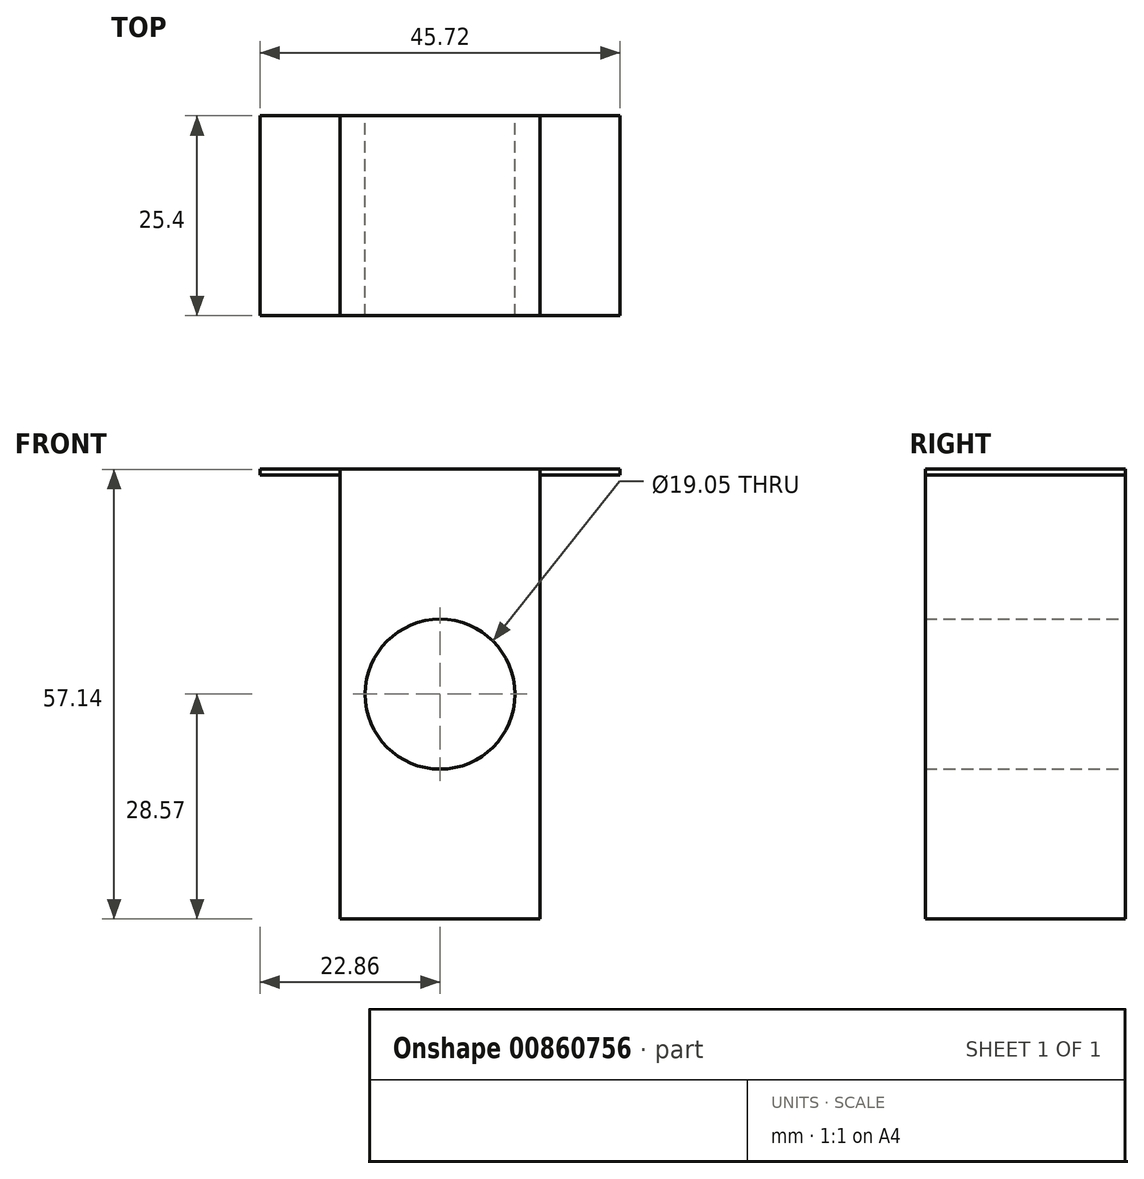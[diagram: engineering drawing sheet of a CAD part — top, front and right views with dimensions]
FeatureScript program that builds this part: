
annotation { "Feature Type Name" : "Feature", "Feature Type Description" : "" }
export const myFeature = defineFeature(function(context is Context, id is Id, definition is map)
    precondition{}
    {
        {
            var Q0;
            Q0=qCreatedBy(makeId("Front.planeOp"),FACE);
            var sketch = newSketch(context, id + "F0", { "sketchPlane" : qUnion([Q0])});
            skLineSegment(sketch, "E0.bottom", {"start": v(12.7, -28.58) * mm, "end": v(-12.7, -28.58) * mm});
            skLineSegment(sketch, "E0.top", {"start": v(12.7, 28.58) * mm, "end": v(-12.7, 28.58) * mm});
            skLineSegment(sketch, "E0.left", {"start": v(12.7, -28.58) * mm, "end": v(12.7, 28.57) * mm});
            skLineSegment(sketch, "E0.right", {"start": v(-12.7, -28.58) * mm, "end": v(-12.7, 28.57) * mm});
            skPoint(sketch, "E0.middle", {"position": v(0, 0) * mm});
            skSolve(sketch);
        }
        {
            var Q0;
            Q0 = qSketchRegion(id + "F0", true);
            extrude(context, id + "F1", {"entities" : qUnion([Q0]), "depth" : 25.4 * mm, "offsetDistance" : 25.4 * mm});
        }
        {
            var Q0;
            Q0=makeQuery(id+"F1.opExtrude","SWEPT_FACE",FACE,{"disambiguationData":[OSD([sQuery(id+"F0.wireOp",EDGE,"E0.top")])]});
            var sketch = newSketch(context, id + "F2", { "sketchPlane" : qUnion([Q0])});
            skLineSegment(sketch, "E1", {"start": v(12.7, 0) * mm, "end": v(22.86, 0) * mm});
            skLineSegment(sketch, "E2", {"start": v(22.86, 0) * mm, "end": v(22.86, -25.4) * mm});
            skLineSegment(sketch, "E3", {"start": v(22.86, -25.4) * mm, "end": v(12.7, -25.4) * mm});
            skLineSegment(sketch, "E4", {"start": v(-12.7, 0) * mm, "end": v(-22.86, 0) * mm});
            skLineSegment(sketch, "E5", {"start": v(-22.86, 0) * mm, "end": v(-22.86, -25.4) * mm});
            skLineSegment(sketch, "E6", {"start": v(-22.86, -25.4) * mm, "end": v(-12.7, -25.4) * mm});
            skSolve(sketch);
        }
        {
            var Q0;
            Q0 = qSketchRegion(id + "F2", true);
            var Q1;
            Q1=makeQuery(id+"F2.imprint","IMPRINT",FACE,{"disambiguationData":[TD([[makeQuery(id+"F2.imprint","IMPRINT",EDGE,{"derivedFrom":sQuery(id+"F2.wireOp",EDGE,"E4")}),1.0]])]});
            var Q2;
            Q2=makeQuery(id+"F2.imprint","IMPRINT",FACE,{"disambiguationData":[TD([[makeQuery(id+"F2.imprint","IMPRINT",EDGE,{"derivedFrom":sQuery(id+"F2.wireOp",EDGE,"E1")}),-1.0]])]});
            extrude(context, id + "F3", {"entities" : qUnion([Q0, Q1, Q2]), "oppositeDirection" : true, "depth" : 0.76 * mm, "offsetDistance" : 25.4 * mm});
        }
        {
            var Q0;
            Q0=makeQuery(id+"F1.opExtrude","CAP_FACE",FACE,{"disambiguationData":[OSD([sQuery(id+"F0.wireOp",EDGE,"E0.bottom"),sQuery(id+"F0.wireOp",EDGE,"E0.top"),sQuery(id+"F0.wireOp",EDGE,"E0.left"),sQuery(id+"F0.wireOp",EDGE,"E0.right")])],"isStart":true});
            var sketch = newSketch(context, id + "F4", { "sketchPlane" : qUnion([Q0])});
            skCircle(sketch, "E7", {"center": v(0, 0) * mm, "radius": 9.53 * mm});
            skSolve(sketch);
        }
        {
            var Q0;
            Q0=makeQuery(id+"F4.imprint","IMPRINT",FACE,{"disambiguationData":[TD([[makeQuery(id+"F4.imprint","IMPRINT",EDGE,{"derivedFrom":sQuery(id+"F4.wireOp",EDGE,"E7")}),1.0]])]});
            extrude(context, id + "F5", {"entities" : qUnion([Q0]), "operationType" : NewBodyOperationType.REMOVE, "oppositeDirection" : true, "depth" : 25.4 * mm, "offsetDistance" : 25.4 * mm});
        }
    });
